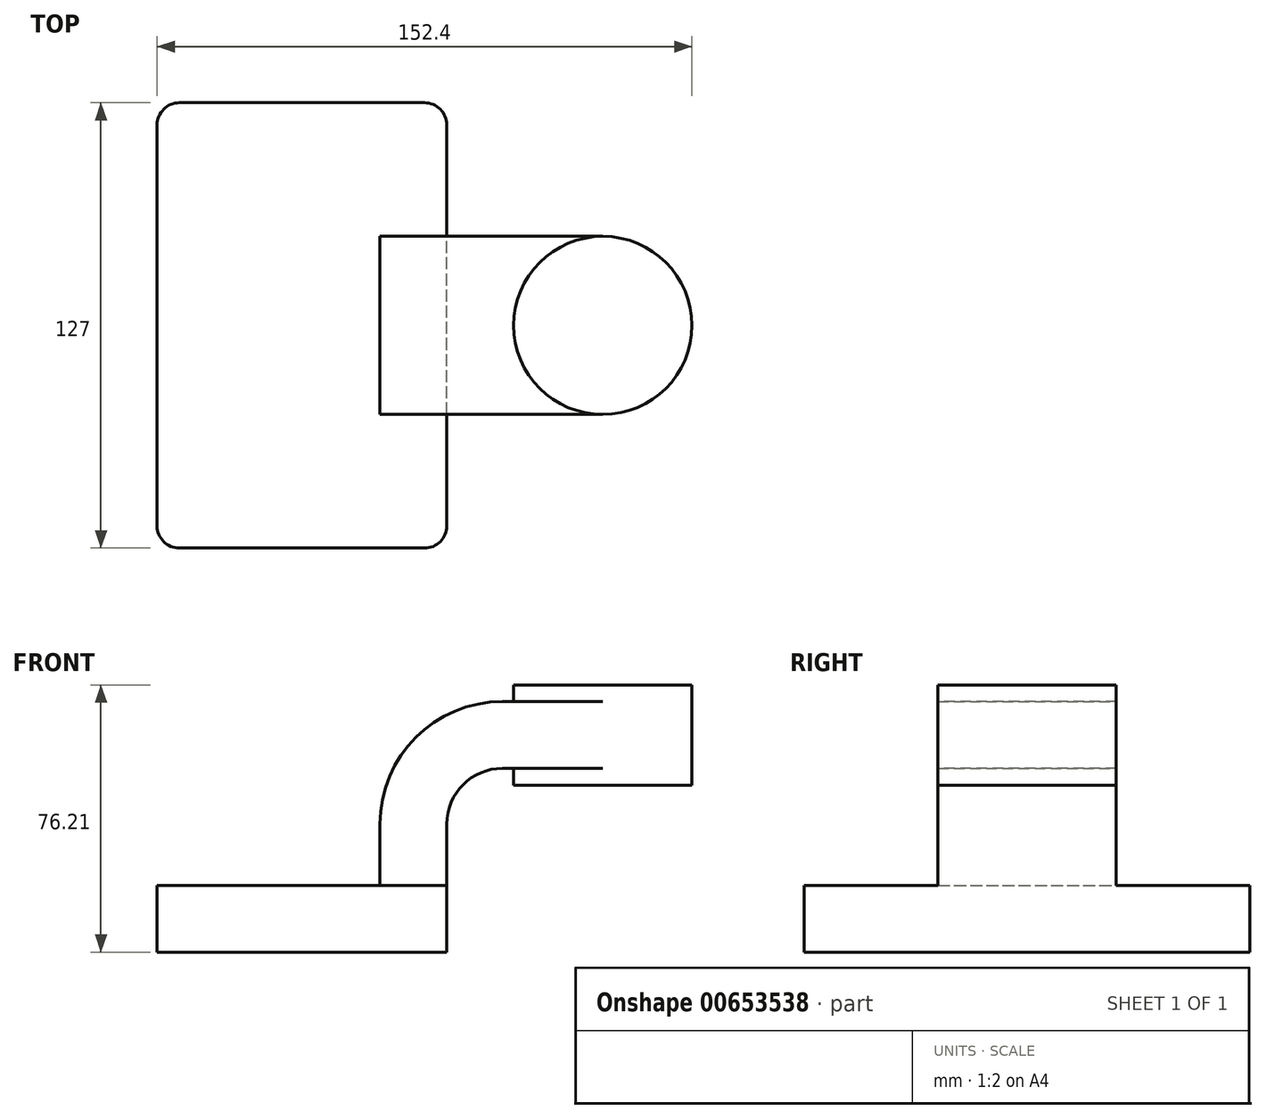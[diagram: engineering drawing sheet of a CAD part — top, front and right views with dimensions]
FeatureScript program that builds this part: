
annotation { "Feature Type Name" : "Feature", "Feature Type Description" : "" }
export const myFeature = defineFeature(function(context is Context, id is Id, definition is map)
    precondition{}
    {
        {
            var Q0;
            Q0=qCreatedBy(makeId("Front.planeOp"),FACE);
            var sketch = newSketch(context, id + "F0", { "sketchPlane" : qUnion([Q0])});
            skLineSegment(sketch, "E0.bottom", {"start": v(41.28, 9.53) * mm, "end": v(-41.28, 9.53) * mm});
            skLineSegment(sketch, "E0.top", {"start": v(41.28, -9.52) * mm, "end": v(-41.28, -9.52) * mm});
            skLineSegment(sketch, "E0.left", {"start": v(41.28, 9.53) * mm, "end": v(41.28, -9.52) * mm});
            skLineSegment(sketch, "E0.right", {"start": v(-41.28, 9.53) * mm, "end": v(-41.28, -9.52) * mm});
            skPoint(sketch, "E0.middle", {"position": v(0, 0) * mm});
            skLineSegment(sketch, "E1.bottom", {"start": v(60.32, 38.1) * mm, "end": v(111.12, 38.1) * mm});
            skLineSegment(sketch, "E1.top", {"start": v(60.32, 66.68) * mm, "end": v(111.12, 66.68) * mm});
            skLineSegment(sketch, "E1.left", {"start": v(60.32, 38.1) * mm, "end": v(60.32, 66.67) * mm});
            skLineSegment(sketch, "E1.right", {"start": v(111.12, 38.1) * mm, "end": v(111.12, 66.68) * mm});
            skPoint(sketch, "E1.middle", {"position": v(85.72, 52.39) * mm});
            skLineSegment(sketch, "E2", {"start": v(41.28, 9.53) * mm, "end": v(41.28, 27) * mm});
            skArc(sketch, "E3", {"start": v(41.28, 27) * mm, "mid": v(45.92, 38.23) * mm, "end": v(57.15, 42.88) * mm});
            skLineSegment(sketch, "E4", {"start": v(57.15, 42.88) * mm, "end": v(85.72, 42.88) * mm});
            skLineSegment(sketch, "E5.0", {"start": v(57.15, 61.93) * mm, "end": v(85.72, 61.93) * mm});
            skArc(sketch, "E5.1", {"start": v(22.23, 27) * mm, "mid": v(32.45, 51.7) * mm, "end": v(57.15, 61.93) * mm});
            skLineSegment(sketch, "E5.2", {"start": v(22.22, 9.53) * mm, "end": v(22.22, 27) * mm});
            skFitSpline(sketch, "E6", {"points": [v(-41.28, 9.53) * mm, v(57.15, 61.93) * mm], "startDerivative": vector(2.7, 102.81) * mm, "endDerivative": vector(109.81, -0.52) * mm});
            skLineSegment(sketch, "E7", {"start": v(85.72, 66.68) * mm, "end": v(85.72, 38.1) * mm});
            skSolve(sketch);
        }
        {
            var Q0;
            Q0=makeQuery(id+"F0.imprint","IMPRINT",FACE,{"disambiguationData":[TD([[makeQuery(id+"F0.imprint","IMPRINT",EDGE,{"derivedFrom":sQuery(id+"F0.wireOp",EDGE,"E0.top")}),-1.0]])]});
            extrude(context, id + "F1", {"entities" : qUnion([Q0]), "endBound" : BoundingType.SYMMETRIC, "depth" : 127 * mm, "offsetDistance" : 25.4 * mm});
        }
        {
            var Q0;
            {var subQ1=sQuery(id+"F0.wireOp",EDGE,"E2");Q0=makeQuery(id+"F0.imprint","IMPRINT",FACE,{"disambiguationData":[TD([[makeQuery(id+"F0.imprint","IMPRINT",EDGE,{"derivedFrom":subQ1}),1.0]])]});}
            var Q1;
            {var subQ0=sQuery(id+"F0.wireOp",EDGE,"E4");var subQ1=sQuery(id+"F0.wireOp",EDGE,"E1.left");var subQ2=makeQuery(id+"F0.imprint","INTERSECT",VERTEX,{"derivedFrom":[subQ1,subQ0]});Q1=makeQuery(id+"F0.imprint","IMPRINT",FACE,{"disambiguationData":[TD([[makeQuery(id+"F0.imprint","IMPRINT",EDGE,{"disambiguationData":[TD([[subQ2,-1.0]])],"derivedFrom":subQ1}),-1.0]])]});}
            extrude(context, id + "F2", {"entities" : qUnion([Q0, Q1]), "operationType" : NewBodyOperationType.ADD, "endBound" : BoundingType.SYMMETRIC, "depth" : 50.8 * mm, "offsetDistance" : 25.4 * mm});
        }
        {
            var Q0;
            Q0=makeQuery(id+"F0.imprint","IMPRINT",FACE,{"disambiguationData":[TD([[makeQuery(id+"F0.imprint","IMPRINT",EDGE,{"derivedFrom":sQuery(id+"F0.wireOp",EDGE,"E5.1")}),1.0]])]});
            extrude(context, id + "F3", {"entities" : qUnion([Q0]), "operationType" : NewBodyOperationType.ADD, "endBound" : BoundingType.SYMMETRIC, "depth" : 15.88 * mm, "offsetDistance" : 25.4 * mm});
        }
        {
            var Q0;
            {var subQ4=sQuery(id+"F0.wireOp",EDGE,"E1.right");Q0=makeQuery(id+"F0.imprint","IMPRINT",FACE,{"disambiguationData":[TD([[makeQuery(id+"F0.imprint","IMPRINT",EDGE,{"derivedFrom":subQ4}),1.0]])]});}
            var Q1;
            Q1=sQuery(id+"F0.wireOp",EDGE,"E7");
            revolve(context, id + "F4", {"operationType" : NewBodyOperationType.ADD, "entities" : qUnion([Q0]), "axis" : qUnion([Q1]), "revolveType" : RevolveType.FULL});
        }
        {
            var Q0;
            Q0=makeQuery(id+"F1.opExtrude","CAP_EDGE",EDGE,{"disambiguationData":[OSD([sQuery(id+"F0.wireOp",EDGE,"E0.right")])],"isStart":false});
            var Q1;
            Q1=makeQuery(id+"F1.opExtrude","CAP_EDGE",EDGE,{"disambiguationData":[OSD([sQuery(id+"F0.wireOp",EDGE,"E0.left")])],"isStart":false});
            var Q2;
            Q2=makeQuery(id+"F1.opExtrude","CAP_EDGE",EDGE,{"disambiguationData":[OSD([sQuery(id+"F0.wireOp",EDGE,"E0.left")])],"isStart":true});
            var Q3;
            Q3=makeQuery(id+"F1.opExtrude","CAP_EDGE",EDGE,{"disambiguationData":[OSD([sQuery(id+"F0.wireOp",EDGE,"E0.right")])],"isStart":true});
            fillet(context, id + "F5", {"entities" : qUnion([Q0, Q1, Q2, Q3]), "radius" : 6.35 * mm, "tangentPropagation" : true, "allowEdgeOverflow" : false});
        }
    });
